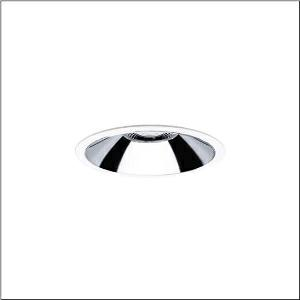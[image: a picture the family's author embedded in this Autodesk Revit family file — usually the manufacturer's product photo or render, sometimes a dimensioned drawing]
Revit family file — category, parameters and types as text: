
# Revit family: lunis_21_xl_51db15df43
name_source: partatom
category: Lighting Fixtures
units: mm (PartAtom-declared; Revit-internal decimal feet)

## family parameters
Cut with Voids When Loaded = No
Host = Face
Light Source = No
Part Type = Normal
Room Calculation Point = No
Round Connector Dimension = Use Diameter
Shared = No

## types (1)
- Lunis 21 XL (1 x LED, 3560 lm, 31 W, 4000K)
    Apparent Load = 31 VA
    CIE Flux Codes = 89 99 100 100 100
    Color Rendering = 80
    Color Temperature = 4000K
    Default Elevation = 1800 mm
    Description = Lunis 21,  XL, downlight, of PC, light emission: direct distribution, LED rated luminous flux: 3.560lm, light colour: 840, control gear: ECG DALI, with terminal, 5-pole, mains connection: 220..240V, AC, housing, round, of diecast aluminium, traffic white (RAL 9016), diameter: 213mm, protection rating (complete): IP20, protection rating (on room side): IP54, insulation class (complete): insulation class II (safety insulation), certification: CE, impact resistance: IK02, packaging unit: 1 piece
    Height = 0 mm  [stored 0 ft]
    Lamp = 1 x LED
    Lamp Light Flux = 3560 lm
    Lamp Power = 31 W
    Lamp count = 1
    Length = 213 mm
    Luminous efficacy = 115 lm/W
    Manufacturer = Siteco
    ModVariant = No
    Model = 51DB15DF43
    Mounting Place = Ceiling
    Mounting Type = Recessed
    Number of Poles = 1
    OnlyDefault = Yes
    Power Factor = 1
    Product Name = Lunis 21 XL
    Product group = downlight
    ProductGroupID = 400
    Protection Class = Protection class II
    Protection Degree = IP 20
    RLX_Detail_Level = 1
    RLX_Emergency_Light_Flux = 0 lm
    RLX_Emergency_Type = 0
    RLX_Emergency_Type_DB = No
    RlxData = <blob elided: 27013 chars, md5=7aa76f98>
    Socket = socket
    Standby Power = 0 W
    System Light Flux = 3560 lm
    System Power = 31 W
    Type Comments = Product without accessories
    Type Image = l_1287385.jpg
    URL = http://relux.com
    VarID = ---
    Voltage = 0 V
    Weight = 0.00 kg
    Width = 0 mm  [stored 0 ft]

note: [stored X ft] marks values corroborated as IEEE doubles in the binary element streams (Revit-internal decimal feet)

## geometry (parser evidence)
native form markers: Blend x4, Sweep x12
no freeform markers — native parametric forms only
